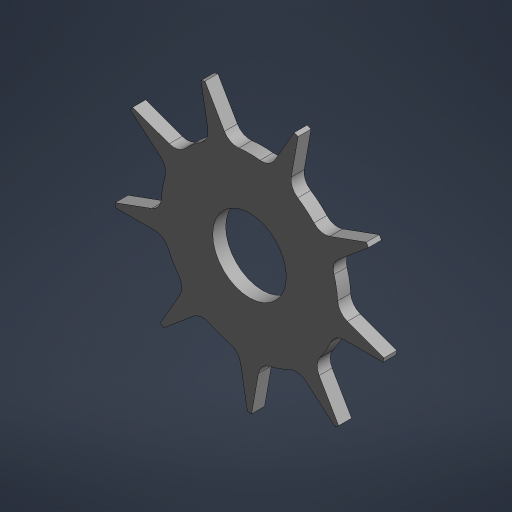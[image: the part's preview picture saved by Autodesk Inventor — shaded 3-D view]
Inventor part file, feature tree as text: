
AUTODESK INVENTOR PART (.ipt)
format: ipt  version: 2023.4 (Build 274418000, 418)  size: 224,256 bytes
history: native  units: mm (DEFAULTED — no unit token found)
features: extrude x2, sketch x2, pattern_circular x1
ambient origin geometry x8: Origin, YZ Plane, XZ Plane, XY Plane, X Axis, Y Axis, Z Axis, Center Point
bodies: Solid7 (feature_tree)
feature tree (5):
  extrude  "Extrusion1"  Depth=26.55325mm
  extrude  "Extrusion2"  Depth=2.794mm TaperAngle=0.0deg
  pattern_circular  "Circular Pattern1"  Angle=60.0deg  [1 undecoded]
  sketch  "Sketch1"  dims[d0=15.875mm d1=26.55325mm]
  sketch  "Sketch2"  dims[d2=58.7375mm d3=2.794mm d4=0.0mm d8=60.0deg d9=19.05mm d10=3.175mm d11=5.334mm d12=0.0mm d13=0.0mm d14=90.0mm d15=360.0deg]
note: 1 required parameter value undecoded (feature->parameter linkage not recoverable at this tier; creation-order binding heuristic only, values carry confidence <= 0.55)
